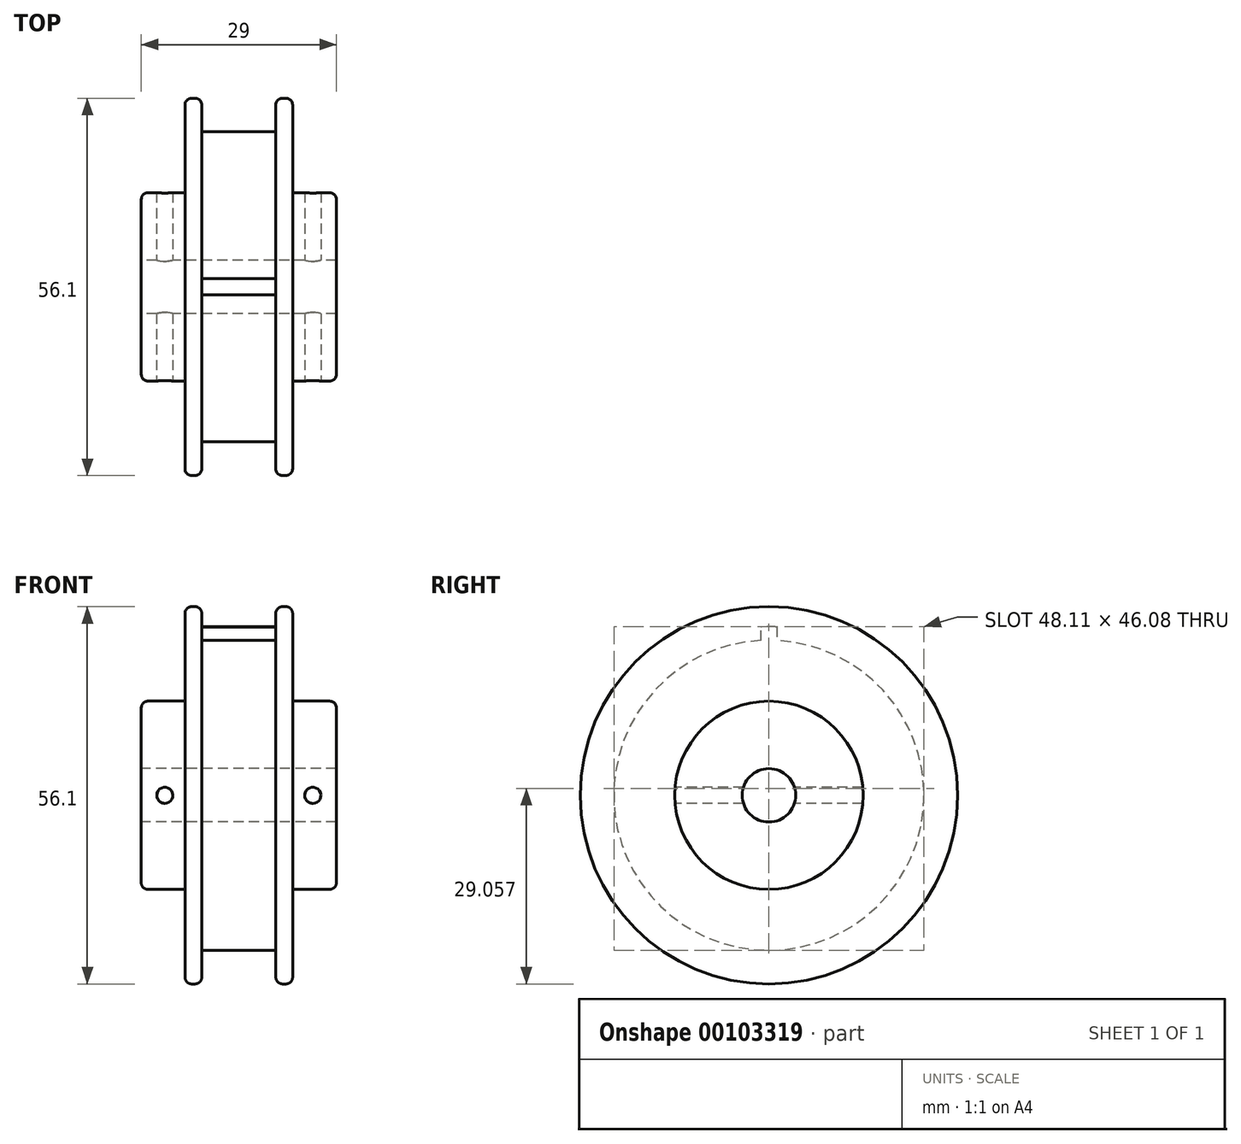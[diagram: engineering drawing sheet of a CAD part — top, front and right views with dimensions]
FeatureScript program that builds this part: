
annotation { "Feature Type Name" : "Feature", "Feature Type Description" : "" }
export const myFeature = defineFeature(function(context is Context, id is Id, definition is map)
    precondition{}
    {
        {
            var Q0;
            Q0=qCreatedBy(makeId("Right.planeOp"),FACE);
            var sketch = newSketch(context, id + "F0", { "sketchPlane" : qUnion([Q0])});
            skCircle(sketch, "E0", {"center": v(0, 0) * mm, "radius": 3.98 * mm});
            skCircle(sketch, "E1", {"center": v(0, 0) * mm, "radius": 14 * mm});
            skSolve(sketch);
        }
        {
            var Q0;
            Q0=makeQuery(id+"F0.imprint","IMPRINT",FACE,{"disambiguationData":[TD([[makeQuery(id+"F0.imprint","IMPRINT",EDGE,{"derivedFrom":sQuery(id+"F0.wireOp",EDGE,"E0")}),-1.0]])]});
            extrude(context, id + "F1", {"entities" : qUnion([Q0]), "endBound" : BoundingType.SYMMETRIC, "depth" : 29 * mm});
        }
        {
            var Q0;
            Q0=qCreatedBy(makeId("Right.planeOp"),FACE);
            var sketch = newSketch(context, id + "F2", { "sketchPlane" : qUnion([Q0])});
            skCircle(sketch, "E2", {"center": v(0, 0) * mm, "radius": 14 * mm});
            skCircle(sketch, "E3", {"center": v(0, 0) * mm, "radius": 23.05 * mm});
            skSolve(sketch);
        }
        {
            var Q0;
            Q0=makeQuery(id+"F2.imprint","IMPRINT",FACE,{"disambiguationData":[TD([[makeQuery(id+"F2.imprint","IMPRINT",EDGE,{"derivedFrom":sQuery(id+"F2.wireOp",EDGE,"E2")}),-1.0]])]});
            extrude(context, id + "F3", {"entities" : qUnion([Q0]), "operationType" : NewBodyOperationType.ADD, "endBound" : BoundingType.SYMMETRIC, "depth" : 16 * mm});
        }
        {
            var Q0;
            Q0=qCreatedBy(makeId("Front.planeOp"),FACE);
            var sketch = newSketch(context, id + "F4", { "sketchPlane" : qUnion([Q0])});
            skLineSegment(sketch, "E4", {"start": v(-27.37, 0) * mm, "end": v(29.66, 0) * mm});
            skLineSegment(sketch, "E5.bottom", {"start": v(-8, 28.05) * mm, "end": v(8, 28.05) * mm});
            skLineSegment(sketch, "E5.top", {"start": v(-8, 23.05) * mm, "end": v(8, 23.05) * mm});
            skLineSegment(sketch, "E5.left", {"start": v(-8, 28.05) * mm, "end": v(-8, 23.05) * mm});
            skLineSegment(sketch, "E5.right", {"start": v(8, 28.05) * mm, "end": v(8, 23.05) * mm});
            skLineSegment(sketch, "E6", {"start": v(-5.5, 28.05) * mm, "end": v(-5.5, 23.05) * mm});
            skLineSegment(sketch, "E7", {"start": v(5.5, 28.05) * mm, "end": v(5.5, 23.05) * mm});
            skSolve(sketch);
        }
        {
            var Q0;
            {var subQ0=sQuery(id+"F4.wireOp",EDGE,"E5.left");Q0=makeQuery(id+"F4.imprint","IMPRINT",FACE,{"disambiguationData":[TD([[makeQuery(id+"F4.imprint","IMPRINT",EDGE,{"derivedFrom":subQ0}),1.0]])]});}
            var Q1;
            {var subQ0=sQuery(id+"F4.wireOp",EDGE,"E5.right");Q1=makeQuery(id+"F4.imprint","IMPRINT",FACE,{"disambiguationData":[TD([[makeQuery(id+"F4.imprint","IMPRINT",EDGE,{"derivedFrom":subQ0}),-1.0]])]});}
            var Q2;
            Q2=sQuery(id+"F4.wireOp",EDGE,"E4");
            revolve(context, id + "F5", {"operationType" : NewBodyOperationType.ADD, "entities" : qUnion([Q0, Q1]), "axis" : qUnion([Q2]), "revolveType" : RevolveType.FULL});
        }
        {
            var Q0;
            {var subQ0=sQuery(id+"F4.wireOp",EDGE,"E6");Q0=makeQuery(id+"F4.imprint","IMPRINT",FACE,{"disambiguationData":[TD([[makeQuery(id+"F4.imprint","IMPRINT",EDGE,{"derivedFrom":subQ0}),1.0]])]});}
            var Q1;
            Q1=sQuery(id+"F4.wireOp",EDGE,"E4");
            revolve(context, id + "F6", {"operationType" : NewBodyOperationType.REMOVE, "entities" : qUnion([Q0]), "axis" : qUnion([Q1]), "revolveType" : RevolveType.FULL, "oppositeDirection" : true});
        }
        {
            var Q0;
            {var subQ0=sQuery(id+"F4.wireOp",EDGE,"E6");Q0=makeQuery(id+"F6.boolean.opBoolean","MERGE",FACE,{"derivedFrom":[makeQuery(id+"F5.opRevolve","SWEPT_FACE",FACE,{"disambiguationData":[OSD([subQ0])]}),makeQuery(id+"F6.opRevolve","SWEPT_FACE",FACE,{"disambiguationData":[OSD([subQ0])]})]});}
            var sketch = newSketch(context, id + "F7", { "sketchPlane" : qUnion([Q0])});
            skArc(sketch, "E8", {"start": v(-1.2, 22.97) * mm, "mid": v(0, -23) * mm, "end": v(1.2, 22.97) * mm, "construction": true});
            skArc(sketch, "E9", {"start": v(1.2, 22.97) * mm, "mid": v(0, 23) * mm, "end": v(-1.2, 22.97) * mm});
            skPoint(sketch, "E10.visualSharp", {"position": v(-1.2, 25.03) * mm});
            skPoint(sketch, "E11.visualSharp", {"position": v(1.2, 25.03) * mm});
            skArc(sketch, "E12", {"start": v(-1.25, 25.03) * mm, "mid": v(0, -25.06) * mm, "end": v(1.27, 25.03) * mm});
            skArc(sketch, "E13", {"start": v(1.27, 25.03) * mm, "mid": v(-0.37, 25.06) * mm, "end": v(-2, 24.98) * mm});
            skLineSegment(sketch, "E14", {"start": v(-1.2, 22.97) * mm, "end": v(-1.2, 25.03) * mm});
            skLineSegment(sketch, "E15", {"start": v(1.2, 25.03) * mm, "end": v(1.2, 22.97) * mm});
            skSolve(sketch);
        }
        {
            var Q0;
            {var subQ0=sQuery(id+"F7.wireOp",EDGE,"E14");var subQ1=sQuery(id+"F7.wireOp",EDGE,"E13");var subQ2=makeQuery(id+"F7.imprint","INTERSECT",VERTEX,{"derivedFrom":[subQ1,subQ0]});Q0=makeQuery(id+"F7.imprint","IMPRINT",FACE,{"disambiguationData":[TD([[makeQuery(id+"F7.imprint","IMPRINT",EDGE,{"disambiguationData":[TD([[subQ2,1.0]])],"derivedFrom":subQ1}),1.0]])]});}
            var Q1;
            Q1=makeQuery(id+"F5.opRevolve","SWEPT_FACE",FACE,{"disambiguationData":[OSD([sQuery(id+"F4.wireOp",EDGE,"E7")])]});
            extrude(context, id + "F8", {"entities" : qUnion([Q0]), "operationType" : NewBodyOperationType.ADD, "endBound" : BoundingType.UP_TO_SURFACE, "endBoundEntityFace" : qUnion([Q1]), "depth" : 10 * mm});
        }
        {
            var Q0;
            Q0=makeQuery(id+"F5.opRevolve","SWEPT_EDGE",EDGE,{"disambiguationData":[OSD([sQuery(id+"F4.wireOp",EDGE,"E5.bottom"),sQuery(id+"F4.wireOp",EDGE,"E6")])]});
            var Q1;
            Q1=makeQuery(id+"F5.opRevolve","SWEPT_EDGE",EDGE,{"disambiguationData":[OSD([sQuery(id+"F4.wireOp",EDGE,"E5.bottom"),sQuery(id+"F4.wireOp",EDGE,"E7")])]});
            var Q2;
            Q2=makeQuery(id+"F1.opExtrude","CAP_EDGE",EDGE,{"disambiguationData":[OSD([sQuery(id+"F0.wireOp",EDGE,"E1")])],"isStart":true});
            var Q3;
            Q3=makeQuery(id+"F1.opExtrude","CAP_EDGE",EDGE,{"disambiguationData":[OSD([sQuery(id+"F0.wireOp",EDGE,"E1")])],"isStart":false});
            var Q4;
            Q4=makeQuery(id+"F5.opRevolve","SWEPT_EDGE",EDGE,{"disambiguationData":[OSD([sQuery(id+"F4.wireOp",EDGE,"E5.bottom"),sQuery(id+"F4.wireOp",EDGE,"E5.left")])]});
            var Q5;
            Q5=makeQuery(id+"F5.opRevolve","SWEPT_EDGE",EDGE,{"disambiguationData":[OSD([sQuery(id+"F4.wireOp",EDGE,"E5.bottom"),sQuery(id+"F4.wireOp",EDGE,"E5.right")])]});
            fillet(context, id + "F9", {"entities" : qUnion([Q0, Q1, Q2, Q3, Q4, Q5]), "radius" : 1 * mm, "tangentPropagation" : true, "allowEdgeOverflow" : false});
        }
        {
            var Q0;
            Q0=qCreatedBy(makeId("Front.planeOp"),FACE);
            var sketch = newSketch(context, id + "F10", { "sketchPlane" : qUnion([Q0])});
            skCircle(sketch, "E16", {"center": v(-11, 0) * mm, "radius": 1.2 * mm});
            skCircle(sketch, "E17", {"center": v(11, 0) * mm, "radius": 1.2 * mm});
            skSolve(sketch);
        }
        {
            var Q0;
            Q0=makeQuery(id+"F10.imprint","IMPRINT",FACE,{"disambiguationData":[TD([[makeQuery(id+"F10.imprint","IMPRINT",EDGE,{"derivedFrom":sQuery(id+"F10.wireOp",EDGE,"E16")}),1.0]])]});
            var Q1;
            Q1=makeQuery(id+"F10.imprint","IMPRINT",FACE,{"disambiguationData":[TD([[makeQuery(id+"F10.imprint","IMPRINT",EDGE,{"derivedFrom":sQuery(id+"F10.wireOp",EDGE,"E17")}),1.0]])]});
            extrude(context, id + "F11", {"entities" : qUnion([Q0, Q1]), "operationType" : NewBodyOperationType.REMOVE, "endBound" : BoundingType.SYMMETRIC, "oppositeDirection" : true, "depth" : 50 * mm});
        }
    });
